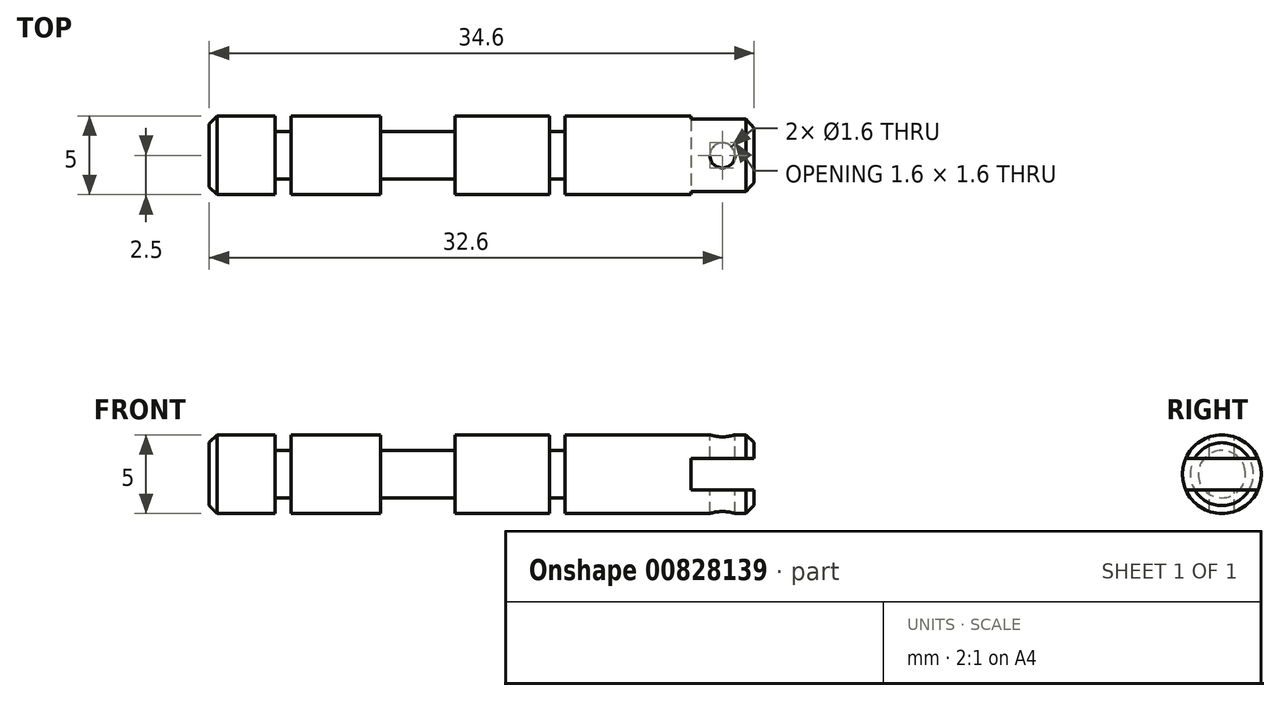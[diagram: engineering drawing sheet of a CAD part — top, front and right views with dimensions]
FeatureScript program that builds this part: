
annotation { "Feature Type Name" : "Feature", "Feature Type Description" : "" }
export const myFeature = defineFeature(function(context is Context, id is Id, definition is map)
    precondition{}
    {
        {
            var Q0;
            Q0=qCreatedBy(makeId("Right.planeOp"),FACE);
            var sketch = newSketch(context, id + "F0", { "sketchPlane" : qUnion([Q0])});
            skCircle(sketch, "E0", {"center": v(0, 0) * mm, "radius": 2.5 * mm});
            skSolve(sketch);
        }
        {
            var Q0;
            Q0 = qSketchRegion(id + "F0", true);
            extrude(context, id + "F1", {"entities" : qUnion([Q0]), "depth" : 34.6 * mm, "offsetDistance" : 25 * mm});
        }
        {
            var Q0;
            Q0=qCreatedBy(makeId("Front.planeOp"),FACE);
            var sketch = newSketch(context, id + "F2", { "sketchPlane" : qUnion([Q0])});
            skLineSegment(sketch, "E1.bottom", {"start": v(4.2, 4.5) * mm, "end": v(5.2, 4.5) * mm});
            skLineSegment(sketch, "E1.top", {"start": v(4.2, 1.5) * mm, "end": v(5.2, 1.5) * mm});
            skLineSegment(sketch, "E1.left", {"start": v(4.2, 4.5) * mm, "end": v(4.2, 1.5) * mm});
            skLineSegment(sketch, "E1.right", {"start": v(5.2, 4.5) * mm, "end": v(5.2, 1.5) * mm});
            skLineSegment(sketch, "E2.bottom", {"start": v(10.9, 4.5) * mm, "end": v(15.6, 4.5) * mm});
            skLineSegment(sketch, "E2.top", {"start": v(10.9, 1.5) * mm, "end": v(15.6, 1.5) * mm});
            skLineSegment(sketch, "E2.left", {"start": v(10.9, 4.5) * mm, "end": v(10.9, 1.5) * mm});
            skLineSegment(sketch, "E2.right", {"start": v(15.6, 4.5) * mm, "end": v(15.6, 1.5) * mm});
            skLineSegment(sketch, "E3.bottom", {"start": v(21.6, 4.5) * mm, "end": v(22.6, 4.5) * mm});
            skLineSegment(sketch, "E3.top", {"start": v(21.6, 1.5) * mm, "end": v(22.6, 1.5) * mm});
            skLineSegment(sketch, "E3.left", {"start": v(21.6, 4.5) * mm, "end": v(21.6, 1.5) * mm});
            skLineSegment(sketch, "E3.right", {"start": v(22.6, 4.5) * mm, "end": v(22.6, 1.5) * mm});
            skLineSegment(sketch, "E4", {"start": v(0, 0) * mm, "end": v(36.91, 0) * mm, "construction": true});
            skSolve(sketch);
        }
        {
            var Q0;
            Q0 = qSketchRegion(id + "F2", true);
            var Q1;
            Q1=sQuery(id+"F2.wireOp",EDGE,"E4");
            revolve(context, id + "F3", {"operationType" : NewBodyOperationType.REMOVE, "surfaceOperationType" : NewSurfaceOperationType.NEW, "entities" : qUnion([Q0]), "axis" : qUnion([Q1]), "revolveType" : RevolveType.FULL, "oppositeDirection" : true});
        }
        {
            var Q0;
            Q0=qCreatedBy(makeId("Front.planeOp"),FACE);
            var sketch = newSketch(context, id + "F4", { "sketchPlane" : qUnion([Q0])});
            skLineSegment(sketch, "E5.bottom", {"start": v(30.6, 1) * mm, "end": v(34.6, 1) * mm});
            skLineSegment(sketch, "E5.top", {"start": v(30.6, -1) * mm, "end": v(34.6, -1) * mm});
            skLineSegment(sketch, "E5.left", {"start": v(30.6, 1) * mm, "end": v(30.6, -1) * mm});
            skLineSegment(sketch, "E5.right", {"start": v(34.6, 1) * mm, "end": v(34.6, -1) * mm});
            skSolve(sketch);
        }
        {
            var Q0;
            Q0 = qSketchRegion(id + "F4", true);
            extrude(context, id + "F5", {"entities" : qUnion([Q0]), "operationType" : NewBodyOperationType.REMOVE, "endBound" : BoundingType.SYMMETRIC, "oppositeDirection" : true, "depth" : 25 * mm, "offsetDistance" : 25 * mm});
        }
        {
            var Q0;
            Q0=qCreatedBy(makeId("Top.planeOp"),FACE);
            var sketch = newSketch(context, id + "F6", { "sketchPlane" : qUnion([Q0])});
            skPoint(sketch, "E6", {"position": v(32.6, 0) * mm});
            skCircle(sketch, "E7", {"center": v(32.6, 0) * mm, "radius": 0.8 * mm});
            skSolve(sketch);
        }
        {
            var Q0;
            Q0 = qSketchRegion(id + "F6", true);
            extrude(context, id + "F7", {"entities" : qUnion([Q0]), "operationType" : NewBodyOperationType.REMOVE, "endBound" : BoundingType.SYMMETRIC, "oppositeDirection" : true, "depth" : 25 * mm, "offsetDistance" : 25 * mm});
        }
        {
            var Q0;
            {var subQ0=sQuery(id+"F0.wireOp",EDGE,"E0");Q0=makeQuery(id+"F5.boolean.opBoolean","SPLIT",EDGE,{"disambiguationData":[TD([makeQuery(id+"F5.opExtrude","SWEPT_FACE",FACE,{"disambiguationData":[OSD([sQuery(id+"F4.wireOp",EDGE,"E5.top")])]})])],"derivedFrom":makeQuery(id+"F1.opExtrude","CAP_EDGE",EDGE,{"disambiguationData":[OSD([subQ0])],"isStart":false})});}
            var Q1;
            {var subQ0=sQuery(id+"F0.wireOp",EDGE,"E0");Q1=makeQuery(id+"F5.boolean.opBoolean","SPLIT",EDGE,{"disambiguationData":[TD([makeQuery(id+"F5.opExtrude","SWEPT_FACE",FACE,{"disambiguationData":[OSD([sQuery(id+"F4.wireOp",EDGE,"E5.bottom")])]})])],"derivedFrom":makeQuery(id+"F1.opExtrude","CAP_EDGE",EDGE,{"disambiguationData":[OSD([subQ0])],"isStart":false})});}
            var Q2;
            Q2=makeQuery(id+"F1.opExtrude","CAP_EDGE",EDGE,{"disambiguationData":[OSD([sQuery(id+"F0.wireOp",EDGE,"E0")])],"isStart":true});
            chamfer(context, id + "F8", {"entities" : qUnion([Q0, Q1, Q2]), "width" : 0.5 * mm, "tangentPropagation" : true});
        }
    });
